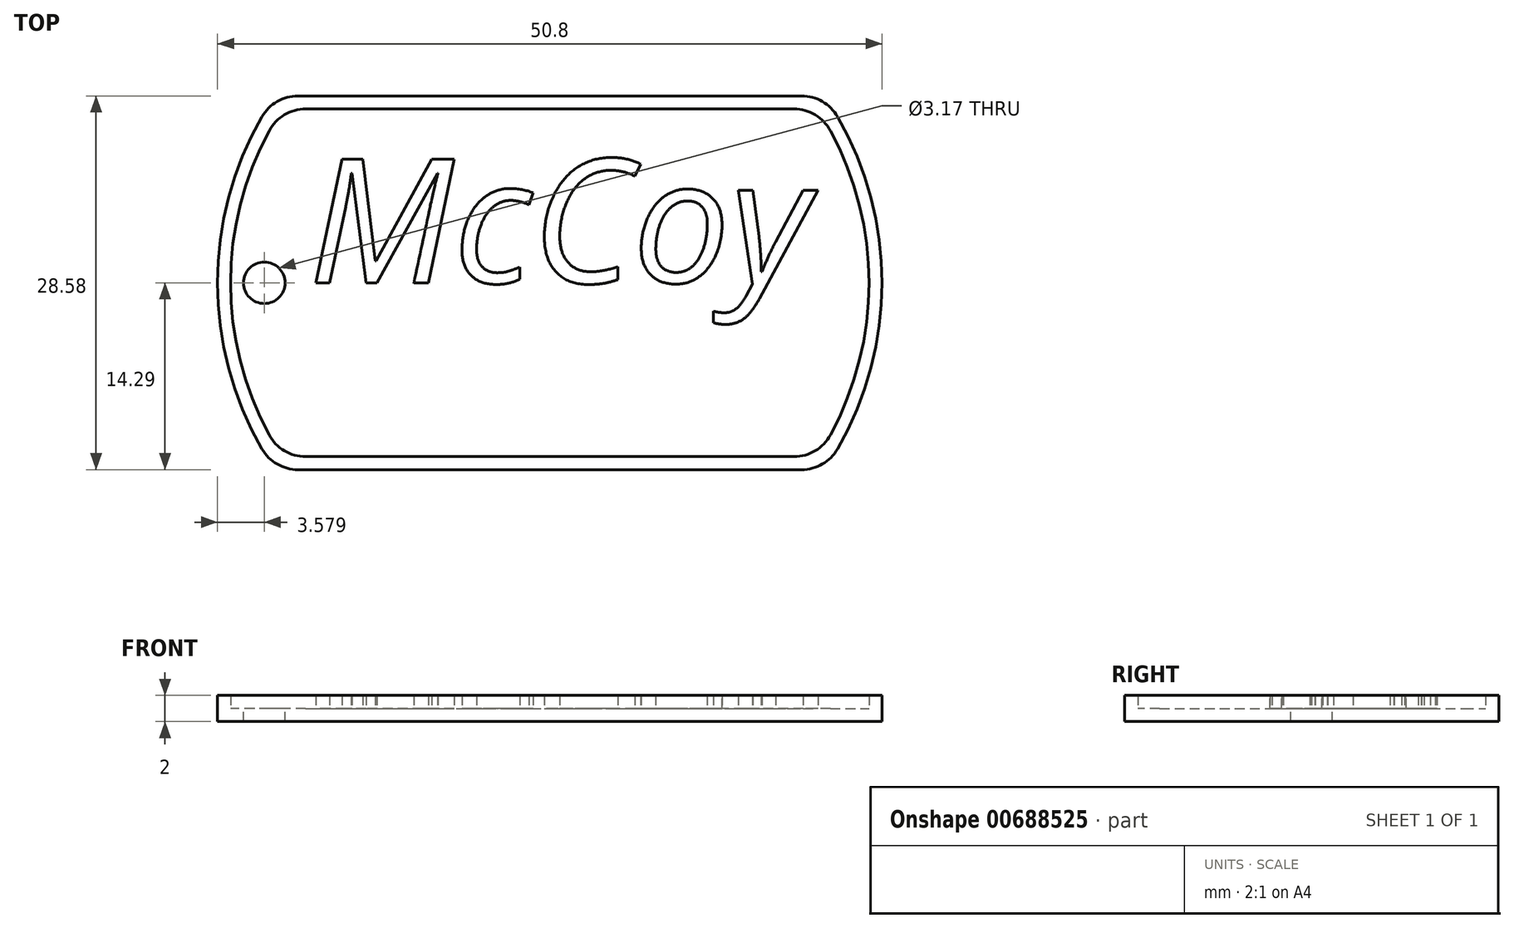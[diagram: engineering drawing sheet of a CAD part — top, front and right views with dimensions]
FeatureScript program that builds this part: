
annotation { "Feature Type Name" : "Feature", "Feature Type Description" : "" }
export const myFeature = defineFeature(function(context is Context, id is Id, definition is map)
    precondition{}
    {
        {
            var Q0;
            Q0=qCreatedBy(makeId("Top.planeOp"),FACE);
            var sketch = newSketch(context, id + "F0", { "sketchPlane" : qUnion([Q0])});
            skArc(sketch, "E0", {"start": v(-22, 12.7) * mm, "mid": v(-25.4, 0) * mm, "end": v(-22, -12.7) * mm});
            skLineSegment(sketch, "E1.top", {"start": v(-19.25, -14.29) * mm, "end": v(19.25, -14.29) * mm});
            skArc(sketch, "E2.trimOffspring", {"start": v(22, -12.7) * mm, "mid": v(25.4, 0) * mm, "end": v(22, 12.7) * mm});
            skLineSegment(sketch, "E3", {"start": v(-19.25, 14.29) * mm, "end": v(19.25, 14.29) * mm});
            skPoint(sketch, "E4.visualSharp", {"position": v(-21, 14.29) * mm});
            skArc(sketch, "E4.filletArc", {"start": v(-19.25, 14.29) * mm, "mid": v(-20.83, 13.86) * mm, "end": v(-22, 12.7) * mm});
            skPoint(sketch, "E5.visualSharp", {"position": v(21, 14.29) * mm});
            skArc(sketch, "E5.filletArc", {"start": v(22, 12.7) * mm, "mid": v(20.83, 13.86) * mm, "end": v(19.25, 14.29) * mm});
            skPoint(sketch, "E6.visualSharp", {"position": v(21, -14.29) * mm});
            skArc(sketch, "E6.filletArc", {"start": v(19.25, -14.29) * mm, "mid": v(20.83, -13.86) * mm, "end": v(22, -12.7) * mm});
            skPoint(sketch, "E7.visualSharp", {"position": v(-21, -14.29) * mm});
            skArc(sketch, "E7.filletArc", {"start": v(-22, -12.7) * mm, "mid": v(-20.83, -13.86) * mm, "end": v(-19.25, -14.29) * mm});
            skSolve(sketch);
        }
        {
            var Q0;
            Q0=makeQuery(id+"F0.imprint","IMPRINT",FACE,{"disambiguationData":[TD([[makeQuery(id+"F0.imprint","IMPRINT",EDGE,{"derivedFrom":sQuery(id+"F0.wireOp",EDGE,"E0")}),1.0]])]});
            extrude(context, id + "F1", {"entities" : qUnion([Q0]), "depth" : 1 * mm, "offsetDistance" : 25.4 * mm});
        }
        {
            var Q0;
            Q0=makeQuery(id+"F1.opExtrude","CAP_FACE",FACE,{"disambiguationData":[OSD([sQuery(id+"F0.wireOp",EDGE,"E0"),sQuery(id+"F0.wireOp",EDGE,"E1.top"),sQuery(id+"F0.wireOp",EDGE,"E2.trimOffspring"),sQuery(id+"F0.wireOp",EDGE,"E3"),sQuery(id+"F0.wireOp",EDGE,"E4.filletArc"),sQuery(id+"F0.wireOp",EDGE,"E5.filletArc"),sQuery(id+"F0.wireOp",EDGE,"E6.filletArc"),sQuery(id+"F0.wireOp",EDGE,"E7.filletArc")])],"isStart":false});
            var sketch = newSketch(context, id + "F2", { "sketchPlane" : qUnion([Q0])});
            skLineSegment(sketch, "E8.0", {"start": v(-18.66, 13.29) * mm, "end": v(18.66, 13.29) * mm});
            skArc(sketch, "E8.1", {"start": v(-21.45, 11.63) * mm, "mid": v(-24.4, 0) * mm, "end": v(-21.45, -11.63) * mm});
            skLineSegment(sketch, "E8.2", {"start": v(-18.66, -13.29) * mm, "end": v(18.66, -13.29) * mm});
            skArc(sketch, "E8.3", {"start": v(21.45, -11.63) * mm, "mid": v(24.4, 0) * mm, "end": v(21.45, 11.63) * mm});
            skPoint(sketch, "E9.visualSharp", {"position": v(-20.46, 13.29) * mm});
            skArc(sketch, "E9.filletArc", {"start": v(-18.66, 13.29) * mm, "mid": v(-20.29, 12.84) * mm, "end": v(-21.45, 11.63) * mm});
            skPoint(sketch, "E10.visualSharp", {"position": v(20.46, 13.29) * mm});
            skArc(sketch, "E10.filletArc", {"start": v(21.45, 11.63) * mm, "mid": v(20.29, 12.84) * mm, "end": v(18.66, 13.29) * mm});
            skPoint(sketch, "E11.visualSharp", {"position": v(20.46, -13.29) * mm});
            skArc(sketch, "E11.filletArc", {"start": v(18.66, -13.29) * mm, "mid": v(20.29, -12.84) * mm, "end": v(21.45, -11.63) * mm});
            skPoint(sketch, "E12.visualSharp", {"position": v(-20.46, -13.29) * mm});
            skArc(sketch, "E12.filletArc", {"start": v(-21.45, -11.63) * mm, "mid": v(-20.29, -12.84) * mm, "end": v(-18.66, -13.29) * mm});
            skLineSegment(sketch, "E13.0", {"start": v(-19.25, 14.29) * mm, "end": v(19.25, 14.29) * mm});
            skArc(sketch, "E13.1", {"start": v(-22, 12.7) * mm, "mid": v(-25.4, 0) * mm, "end": v(-22, -12.7) * mm});
            skLineSegment(sketch, "E13.2", {"start": v(-19.25, -14.29) * mm, "end": v(19.25, -14.29) * mm});
            skArc(sketch, "E13.3", {"start": v(22, -12.7) * mm, "mid": v(25.4, 0) * mm, "end": v(22, 12.7) * mm});
            skPoint(sketch, "E14.visualSharp", {"position": v(-21, -14.29) * mm});
            skArc(sketch, "E14.filletArc", {"start": v(-22, -12.7) * mm, "mid": v(-20.83, -13.86) * mm, "end": v(-19.25, -14.29) * mm});
            skPoint(sketch, "E15.visualSharp", {"position": v(21, -14.29) * mm});
            skArc(sketch, "E15.filletArc", {"start": v(19.25, -14.29) * mm, "mid": v(20.83, -13.86) * mm, "end": v(22, -12.7) * mm});
            skPoint(sketch, "E16.visualSharp", {"position": v(21, 14.29) * mm});
            skArc(sketch, "E16.filletArc", {"start": v(22, 12.7) * mm, "mid": v(20.83, 13.86) * mm, "end": v(19.25, 14.29) * mm});
            skPoint(sketch, "E17.visualSharp", {"position": v(-21, 14.29) * mm});
            skArc(sketch, "E17.filletArc", {"start": v(-19.25, 14.29) * mm, "mid": v(-20.83, 13.86) * mm, "end": v(-22, 12.7) * mm});
            skSolve(sketch);
        }
        {
            var Q0;
            Q0=makeQuery(id+"F2.imprint","IMPRINT",FACE,{"disambiguationData":[TD([[makeQuery(id+"F2.imprint","IMPRINT",EDGE,{"derivedFrom":sQuery(id+"F2.wireOp",EDGE,"E8.0")}),1.0]])]});
            extrude(context, id + "F3", {"entities" : qUnion([Q0]), "operationType" : NewBodyOperationType.ADD, "depth" : 1 * mm, "offsetDistance" : 25.4 * mm});
        }
        {
            var Q0;
            Q0=makeQuery(id+"F1.opExtrude","CAP_FACE",FACE,{"disambiguationData":[OSD([sQuery(id+"F0.wireOp",EDGE,"E0"),sQuery(id+"F0.wireOp",EDGE,"E1.top"),sQuery(id+"F0.wireOp",EDGE,"E2.trimOffspring"),sQuery(id+"F0.wireOp",EDGE,"E3"),sQuery(id+"F0.wireOp",EDGE,"E4.filletArc"),sQuery(id+"F0.wireOp",EDGE,"E5.filletArc"),sQuery(id+"F0.wireOp",EDGE,"E6.filletArc"),sQuery(id+"F0.wireOp",EDGE,"E7.filletArc")])],"isStart":false});
            var sketch = newSketch(context, id + "F4", { "sketchPlane" : qUnion([Q0])});
            skCircle(sketch, "E18", {"center": v(-21.82, 0) * mm, "radius": 1.59 * mm});
            skSolve(sketch);
        }
        {
            var Q0;
            Q0=makeQuery(id+"F4.imprint","IMPRINT",FACE,{"disambiguationData":[TD([[makeQuery(id+"F4.imprint","IMPRINT",EDGE,{"derivedFrom":sQuery(id+"F4.wireOp",EDGE,"E18")}),1.0]])]});
            extrude(context, id + "F5", {"entities" : qUnion([Q0]), "operationType" : NewBodyOperationType.REMOVE, "oppositeDirection" : true, "depth" : 1 * mm, "offsetDistance" : 25.4 * mm});
        }
        {
            var Q0;
            Q0=makeQuery(id+"F2.imprint","IMPRINT",FACE,{"disambiguationData":[TD([[makeQuery(id+"F2.imprint","IMPRINT",EDGE,{"derivedFrom":sQuery(id+"F2.wireOp",EDGE,"E8.0")}),-1.0]])]});
            var sketch = newSketch(context, id + "F6", { "sketchPlane" : qUnion([Q0])});
            skText(sketch, "E19", { "text": "McCoy", "fontName": "OpenSans-Italic.ttf"});
            const initialGuessF6  = {"E19": [-0.01842, 0, 1, 0, 0.00953]};
            skSetInitialGuess(sketch, initialGuessF6);
            skSolve(sketch);
        }
        {
            var Q0;
            Q0=qSketchRegion(id+"F6",true);
            extrude(context, id + "F7", {"entities" : qUnion([Q0]), "operationType" : NewBodyOperationType.ADD, "depth" : 1 * mm, "offsetDistance" : 25.4 * mm});
        }
    });
